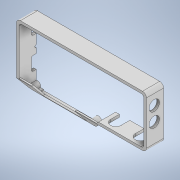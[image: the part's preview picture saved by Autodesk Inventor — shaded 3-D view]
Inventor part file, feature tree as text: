
AUTODESK INVENTOR PART (.ipt)
format: ipt  version: 2021 (Build 250183000, 183)  size: 561,664 bytes
history: native  units: mm
features: sketch x25, extrude x24, fillet x5, chamfer x5, hole x1
ambient origin geometry x8: Origin, YZ Plane, XZ Plane, XY Plane, X Axis, Y Axis, Z Axis, Center Point
bodies: Solid1 (feature_tree)
feature tree (60):
  extrude  "Extrusion1"  Depth=100.0mm
  extrude  "Extrusion3"  Depth=50.0mm
  extrude  "Extrusion4"  Depth=12.5mm
  extrude  "Extrusion12"  Depth=3.0mm TaperAngle=0.0deg
  extrude  "Extrusion13"  Depth=3.0mm TaperAngle=0.0deg
  fillet  "Fillet3"  Radius=2.0mm
  extrude  "Extrusion15"  Depth=2.0mm
  extrude  "Extrusion20"  Depth=1.2mm
  extrude  "Extrusion21"  Depth=12.0mm TaperAngle=0.0deg
  extrude  "Extrusion22"  Depth=2.0mm
  extrude  "Extrusion23"  Depth=3.0mm
  extrude  "Extrusion26"  Depth=4.4mm TaperAngle=0.0deg
  hole  "Hole2"  [1 undecoded]
  chamfer  "Chamfer6"  Distance=12.0mm
  chamfer  "Chamfer7"  Distance=12.0mm
  extrude  "Extrusion27"  Depth=8.0mm
  fillet  "Fillet4"  Radius=8.0mm
  extrude  "Extrusion28"  Depth=2.0mm TaperAngle=0.0deg
  extrude  "Extrusion29"  Depth=6.0mm
  extrude  "Extrusion30"  Depth=6.0mm
  fillet  "Fillet5"  Radius=8.0mm
  extrude  "Extrusion34"  Depth=2.0mm TaperAngle=0.0deg
  extrude  "Extrusion35"  Depth=3.0mm
  extrude  "Extrusion36"  Depth=50.0mm
  extrude  "Extrusion37"  Depth=3.0mm
  fillet  "Fillet6"  Radius=3.0mm
  extrude  "Extrusion38"  Depth=3.0mm
  extrude  "Extrusion39"  Depth=4.8mm
  chamfer  "Chamfer8"  Distance=4.8mm
  extrude  "Extrusion40"  Depth=6.0mm TaperAngle=0.0deg
  fillet  "Fillet7"  Radius=2.0mm
  extrude  "Extrusion41"  Depth=0.8mm TaperAngle=45.0deg
  chamfer  "Chamfer9"  Distance=68.0mm
  chamfer  "Chamfer10"  Distance=2.0mm
  extrude  "Extrusion42"  Depth=2.0mm
  sketch  "Sketch1"  dims[d0=52.0mm d1=100.0mm]
  sketch  "Sketch4"  dims[d2=26.0mm d3=50.0mm]
  sketch  "Sketch5"  dims[d4=1.2mm d5=0.0mm d35=12.5mm]
  sketch  "Sketch13"  dims[d36=63.1mm d37=3.0mm d38=0.0mm]
  sketch  "Sketch14"  dims[d39=50.673mm d40=3.0mm d41=0.0mm d79=2.0mm]
  sketch  "Sketch16"  dims[d80=2.0mm d81=2.0mm]
  sketch  "Sketch21"  dims[d82=1.2mm d83=44.0mm]
  sketch  "Sketch22"  dims[d84=59.0mm d85=12.0mm d86=0.0mm]
  sketch  "Sketch23"  dims[d87=2.0mm d88=12.6mm]
  sketch  "Sketch24"  dims[d89=12.0mm d90=0.0mm d91=3.0mm]
  sketch  "Sketch27"  dims[d95=33.8mm d96=4.4mm d97=0.0mm]
  sketch  "Sketch28"  dims[d117=2.0mm d118=2.0mm d119=12.0mm d120=0.0mm d121=12.0mm d122=0.0mm]
  sketch  "Sketch29"  dims[d123=70.0mm d124=89.0mm d125=8.0mm]
  sketch  "Sketch30"  dims[d126=8.0mm d127=2.0mm d128=0.0mm]
  sketch  "Sketch31"  dims[d129=6.0mm d130=11.0mm]
  sketch  "Sketch32"  dims[d131=11.0mm d132=6.0mm d133=8.0mm]
  sketch  "Sketch36"  dims[d134=8.0mm d135=2.0mm d136=0.0mm]
  sketch  "Sketch37"  dims[d144=3.0mm d145=3.0mm]
  sketch  "Sketch38"  dims[d146=3.0mm d147=50.0mm]
  sketch  "Sketch39"  dims[d148=97.0mm d149=15.0mm d150=3.0mm]
  sketch  "Sketch40"  dims[d151=3.0mm d152=97.0mm]
  sketch  "Sketch41"  dims[d153=49.0mm d154=4.8mm]
  sketch  "Sketch43"  dims[d155=4.8mm]
  sketch  "Sketch44"  dims[d156=4.8mm]
  sketch  "Sketch45"  dims[d157=4.8mm d158=4.8mm d159=6.0mm d160=0.0mm d161=2.0mm d162=6.0mm d163=4.0mm d164=2.0mm d165=90.0deg d166=4.0mm d167=20.594885mm d177=2.0mm d178=2.0mm d179=45.0deg d180=0.8mm d181=2.0mm d182=45.0deg d184=68.0mm d189=2.0mm d190=0.0mm d191=2.0mm d192=2.0mm d193=24.0mm d194=2.0mm d195=0.0mm d196=36.5mm d197=46.5mm d198=3.5mm d199=2.0mm d200=0.0mm d201=12.5mm d202=23.0mm d203=3.5mm d204=2.0mm d205=0.0mm d206=1.0mm d217=7.6mm d218=10.0mm d219=46.4mm d220=20.0mm d221=0.0mm d222=22.68928mm d223=67.0mm d224=0.0mm d225=1.2mm d226=0.0mm d227=1.2mm d228=0.0mm d229=3.0mm d230=12.3mm d231=33.2mm d232=1.0mm d233=10.0mm d234=1.2mm d235=0.0mm d236=1.2mm d237=5.0mm d238=20.0mm d239=1.5mm d240=0.0mm d241=1.5mm d242=2.0mm d243=45.0deg d245=1.2mm d246=0.0mm d247=2.0mm d248=5.0mm d249=0.0mm d250=0.8mm d251=2.0mm d252=45.0deg d253=0.6mm d254=2.0mm d255=45.0deg d256=5.0mm d257=0.0mm d258=2.0mm d259=0.0mm d67=0.5mm d68=0.872665mm d69=0.5mm d70=0.872665mm d71=0.5mm d72=0.872665mm d73=0.5mm d74=0.872665mm d75=0.872665mm d76=0.5mm d77=0.872665mm d208=0.5mm d209=0.872665mm d210=0.5mm d211=0.872665mm d262=0.5mm d263=0.872665mm d264=0.5mm d265=0.872665mm]
note: 1 required parameter value undecoded (feature->parameter linkage not recoverable at this tier; creation-order binding heuristic only, values carry confidence <= 0.55)
